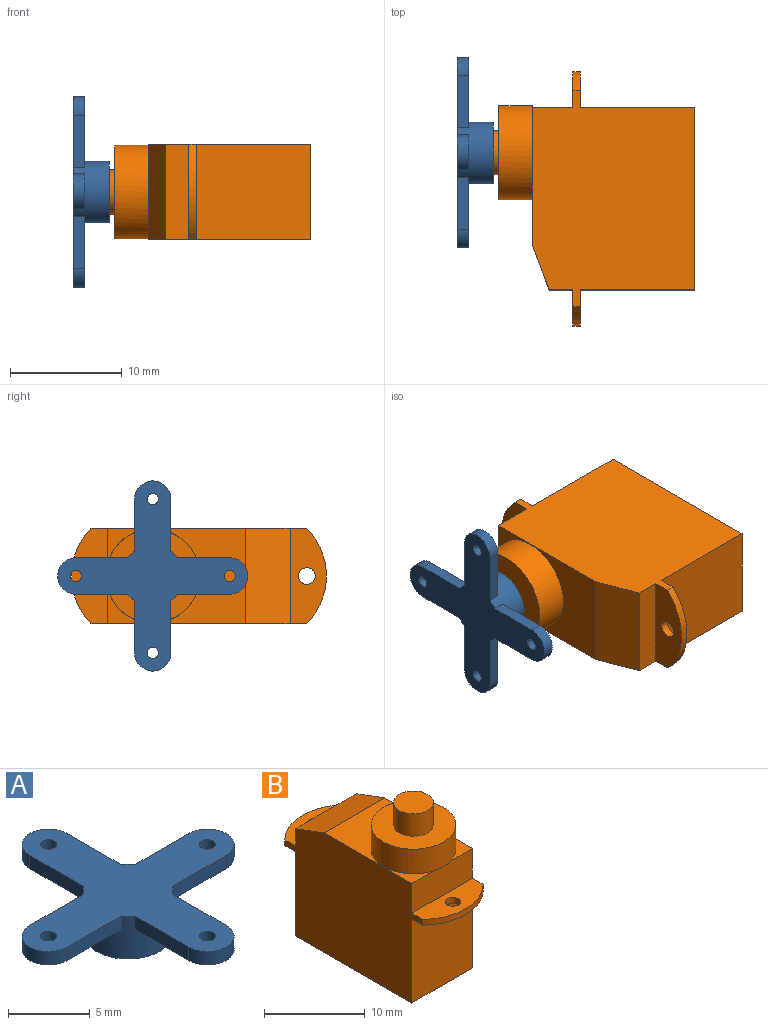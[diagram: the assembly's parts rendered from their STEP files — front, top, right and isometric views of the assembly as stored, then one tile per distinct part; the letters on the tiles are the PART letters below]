
ASSEMBLY  parts=2 mates=1
PART A: 25 faces, bbox 17x17x3.2 mm
  f0: plane 4.66x1mm, normal (-1,0,0), area 4.7mm2, adj f4,f5,f10,f11
  f1: plane 4.66x1mm, normal (-1,0,0), area 4.7mm2, adj f7,f9,f10,f11
  f2: plane 4.66x1mm, normal (1,0,0), area 4.7mm2, adj f4,f5,f10,f11
  f3: plane 4.66x1mm, normal (1,0,0), area 4.7mm2, adj f7,f9,f10,f11
  f4: plane 6.28x3.25mm, normal (0,0,-1), area 17.3mm2, adj f0,f2,f5,f6,f11
  f5: cylinder r=1.62mm len=3.25mm, axis (0,0,1), area 5.1mm2, adj f0,f2,f4,f10
  f6: cylinder r=0.5mm len=1mm, axis (0,0,1), area 3.1mm2, adj f4,f10
  f7: cylinder r=1.62mm len=3.25mm, axis (0,0,1), area 5.1mm2, adj f1,f3,f9,f10
  f8: cylinder r=0.5mm len=1mm, axis (0,0,1), area 3.1mm2, adj f9,f10
  f9: plane 6.28x3.25mm, normal (0,0,-1), area 17.3mm2, adj f1,f3,f7,f8,f11
  f10: plane 17x17mm, normal (0,0,1), area 93mm2, adj f0,f1,f2,f3,f5,f6,f7,f8
  f11: cylinder r=2.75mm len=5.5mm, axis (0,0,-1), area 41.4mm2, adj f0,f1,f2,f3,f4,f9,f10,f12
  f12: plane 4.66x1mm, normal (0,1,0), area 4.7mm2, adj f10,f11,f16,f17
  f13: plane 4.66x1mm, normal (0,1,0), area 4.7mm2, adj f10,f11,f19,f21
  f14: plane 4.66x1mm, normal (0,-1,0), area 4.7mm2, adj f10,f11,f16,f17
  f15: plane 4.66x1mm, normal (0,-1,0), area 4.7mm2, adj f10,f11,f19,f21
  f16: plane 6.28x3.25mm, normal (0,0,-1), area 17.3mm2, adj f11,f12,f14,f17,f18
  f17: cylinder r=1.62mm len=3.25mm, axis (0,0,1), area 5.1mm2, adj f10,f12,f14,f16
  f18: cylinder r=0.5mm len=1mm, axis (0,0,1), area 3.1mm2, adj f10,f16
  f19: cylinder r=1.62mm len=3.25mm, axis (0,0,1), area 5.1mm2, adj f10,f13,f15,f21
  f20: cylinder r=0.5mm len=1mm, axis (0,0,1), area 3.1mm2, adj f10,f21
  f21: plane 6.28x3.25mm, normal (0,0,-1), area 17.3mm2, adj f11,f13,f15,f19,f20
  f22: plane 5.5x5.5mm, normal (0,0,-1), area 11.5mm2, adj f11,f23
  f23: cylinder r=1.98mm len=3.95mm, axis (0,0,-1), area 27.3mm2, adj f22,f24
  f24: plane 3.95x3.95mm, normal (0,0,-1), area 12.3mm2, adj f23
PART B: 22 faces, bbox 8.5x22.8x20.2 mm
  f0: plane 8.5x2.1mm, normal (0,1,0), area 17.8mm2, adj f1,f2,f14,f16
  f1: plane 19.3x14.5mm, normal (1,0,0), area 235.5mm2, adj f0,f3,f4,f5,f6,f7,f8,f10
  f2: plane 19.3x14.5mm, normal (-1,0,0), area 235.5mm2, adj f0,f3,f4,f5,f6,f7,f8,f10
  f3: plane 12.3x8.5mm, normal (0,0,1), area 49.4mm2, adj f1,f2,f4,f16,f17
  f4: plane 8.5x3.6mm, normal (0,-1,0), area 30.6mm2, adj f1,f2,f3,f10,f19
  f5: plane 10.2x8.5mm, normal (0,1,0), area 86.7mm2, adj f1,f2,f7,f15
  f6: plane 10.2x8.5mm, normal (0,-1,0), area 86.7mm2, adj f1,f2,f7,f11
  f7: plane 16.3x8.5mm, normal (0,0,-1), area 138.6mm2, adj f1,f2,f5,f6
  f8: cylinder r=6.04mm len=8.5mm, axis (0,0,-1), area 6.6mm2, adj f1,f2,f10,f11
  f9: cylinder r=0.75mm len=1.5mm, axis (0,0,-1), area 3.3mm2, adj f10,f11
  f10: plane 8.5x3.25mm, normal (0,0,1), area 21.2mm2, adj f1,f2,f4,f8,f9
  f11: plane 8.5x3.25mm, normal (0,0,-1), area 21.2mm2, adj f1,f2,f6,f8,f9
  f12: cylinder r=0.75mm len=1.5mm, axis (0,0,-1), area 3.3mm2, adj f14,f15
  f13: cylinder r=6.04mm len=8.5mm, axis (0,0,-1), area 6.6mm2, adj f1,f2,f14,f15
  f14: plane 8.5x3.25mm, normal (0,0,1), area 21.2mm2, adj f0,f1,f2,f12,f13
  f15: plane 8.5x3.25mm, normal (0,0,-1), area 21.2mm2, adj f1,f2,f5,f12,f13
  f16: plane 8.5x4mm, normal (0,0.35,0.94), area 36.3mm2, adj f0,f1,f2,f3
  f17: cylinder r=4.2mm len=8.4mm, axis (0,0,-1), area 79.2mm2, adj f3,f18,f19
  f18: plane 8.4x8.4mm, normal (0,0,1), area 43.2mm2, adj f17,f20
  f19: plane 2.4x0.18mm, normal (0,0,-1), area 0.3mm2, adj f4,f17
  f20: cylinder r=1.98mm len=3.95mm, axis (0,0,-1), area 33.5mm2, adj f18,f21
  f21: plane 3.95x3.95mm, normal (0,0,1), area 12.3mm2, adj f20
PLACE A rot(axis=(0,-1,0),90deg) t=(11.96,4.14,4.78)mm
PLACE B rot(axis=(0.71,0,-0.71),180deg) t=(11.96,-4.11,4.78)mm fixed
MATE revolute A.f11 <-> B.f17  axis (1,0,0) through (-8.24,0.02,4.78)mm
